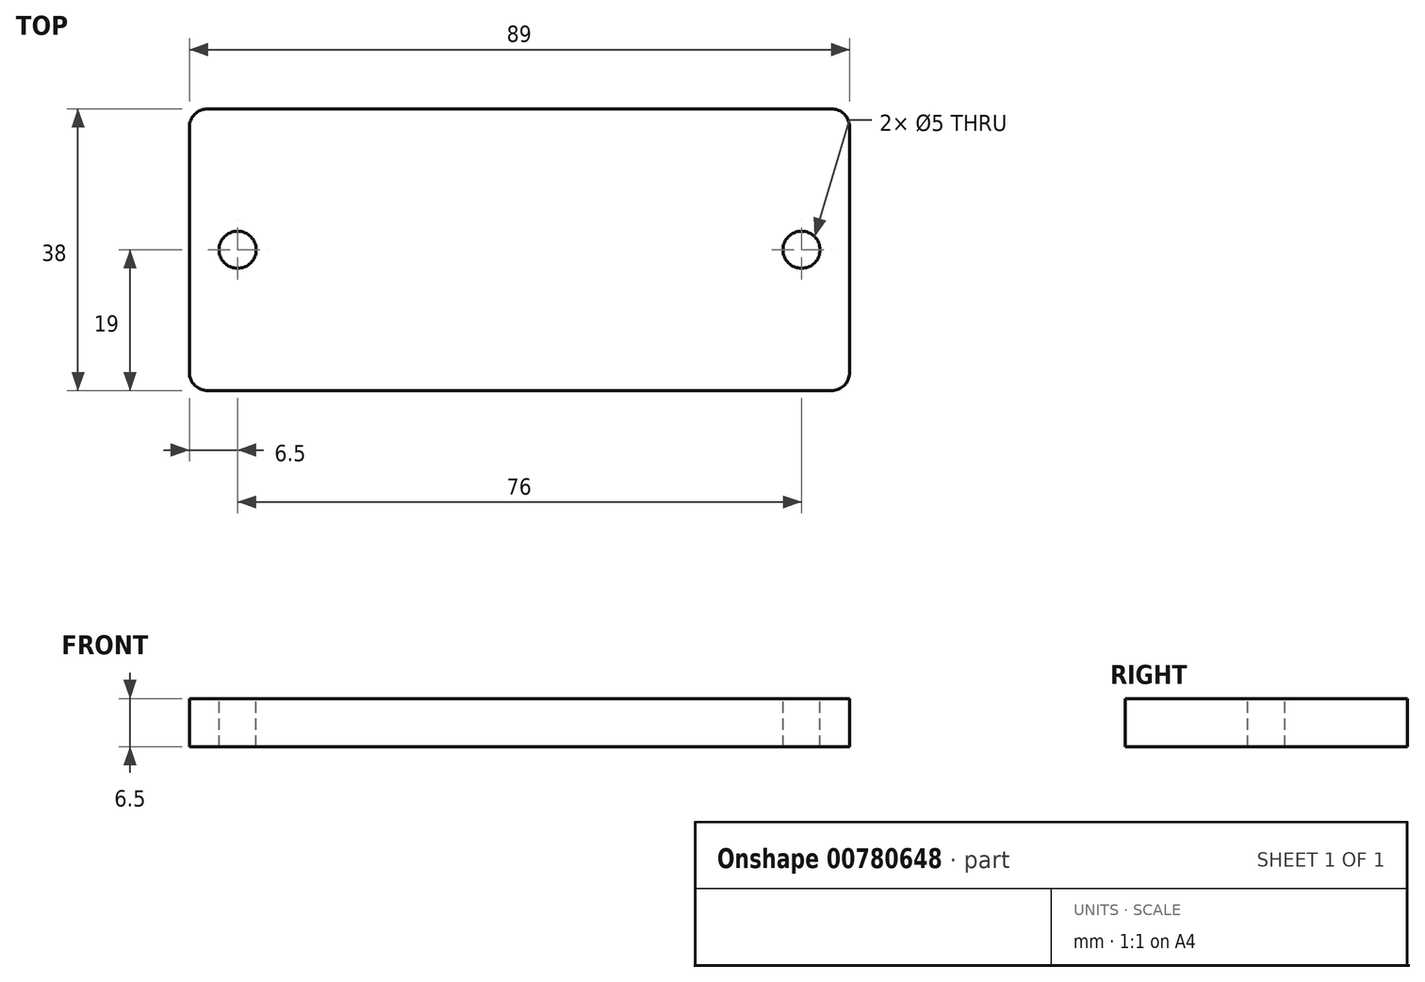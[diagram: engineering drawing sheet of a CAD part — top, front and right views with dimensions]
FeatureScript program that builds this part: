
annotation { "Feature Type Name" : "Feature", "Feature Type Description" : "" }
export const myFeature = defineFeature(function(context is Context, id is Id, definition is map)
    precondition{}
    {
        {
            var Q0;
            Q0=qCreatedBy(makeId("Top.planeOp"),FACE);
            var sketch = newSketch(context, id + "F0", { "sketchPlane" : qUnion([Q0])});
            skLineSegment(sketch, "E0.bottom", {"start": v(42, -19) * mm, "end": v(-42, -19) * mm});
            skLineSegment(sketch, "E0.top", {"start": v(42, 19) * mm, "end": v(-42, 19) * mm});
            skLineSegment(sketch, "E0.left", {"start": v(44.5, -16.5) * mm, "end": v(44.5, 16.5) * mm});
            skLineSegment(sketch, "E0.right", {"start": v(-44.5, -16.5) * mm, "end": v(-44.5, 16.5) * mm});
            skPoint(sketch, "E0.middle", {"position": v(0, 0) * mm});
            skPoint(sketch, "E1.visualSharp", {"position": v(-44.5, 19) * mm});
            skArc(sketch, "E1.filletArc", {"start": v(-42, 19) * mm, "mid": v(-43.77, 18.27) * mm, "end": v(-44.5, 16.5) * mm});
            skPoint(sketch, "E2.visualSharp", {"position": v(44.5, 19) * mm});
            skArc(sketch, "E2.filletArc", {"start": v(44.5, 16.5) * mm, "mid": v(43.77, 18.27) * mm, "end": v(42, 19) * mm});
            skPoint(sketch, "E3.visualSharp", {"position": v(44.5, -19) * mm});
            skArc(sketch, "E3.filletArc", {"start": v(42, -19) * mm, "mid": v(43.77, -18.27) * mm, "end": v(44.5, -16.5) * mm});
            skPoint(sketch, "E4.visualSharp", {"position": v(-44.5, -19) * mm});
            skArc(sketch, "E4.filletArc", {"start": v(-44.5, -16.5) * mm, "mid": v(-43.77, -18.27) * mm, "end": v(-42, -19) * mm});
            skSolve(sketch);
        }
        {
            var Q0;
            Q0 = qSketchRegion(id + "F0", true);
            extrude(context, id + "F1", {"entities" : qUnion([Q0]), "endBound" : BoundingType.SYMMETRIC, "depth" : 6.5 * mm, "offsetDistance" : 25 * mm});
        }
        {
            var Q0;
            Q0=makeQuery(id+"F1.opExtrude","CAP_FACE",FACE,{"disambiguationData":[OSD([sQuery(id+"F0.wireOp",EDGE,"E0.bottom"),sQuery(id+"F0.wireOp",EDGE,"E0.top"),sQuery(id+"F0.wireOp",EDGE,"E0.left"),sQuery(id+"F0.wireOp",EDGE,"E0.right"),sQuery(id+"F0.wireOp",EDGE,"E1.filletArc"),sQuery(id+"F0.wireOp",EDGE,"E2.filletArc"),sQuery(id+"F0.wireOp",EDGE,"E3.filletArc"),sQuery(id+"F0.wireOp",EDGE,"E4.filletArc")])],"isStart":false});
            var sketch = newSketch(context, id + "F2", { "sketchPlane" : qUnion([Q0])});
            skLineSegment(sketch, "E5", {"start": v(0, 0) * mm, "end": v(-38, 0) * mm});
            skLineSegment(sketch, "E6", {"start": v(0, 0) * mm, "end": v(38, 0) * mm});
            skCircle(sketch, "E7", {"center": v(-38, 0) * mm, "radius": 2.5 * mm});
            skCircle(sketch, "E8", {"center": v(38, 0) * mm, "radius": 2.5 * mm});
            skSolve(sketch);
        }
        {
            var Q0;
            Q0 = qSketchRegion(id + "F2", true);
            extrude(context, id + "F3", {"entities" : qUnion([Q0]), "operationType" : NewBodyOperationType.REMOVE, "oppositeDirection" : true, "depth" : 25 * mm, "offsetDistance" : 25 * mm});
        }
    });
